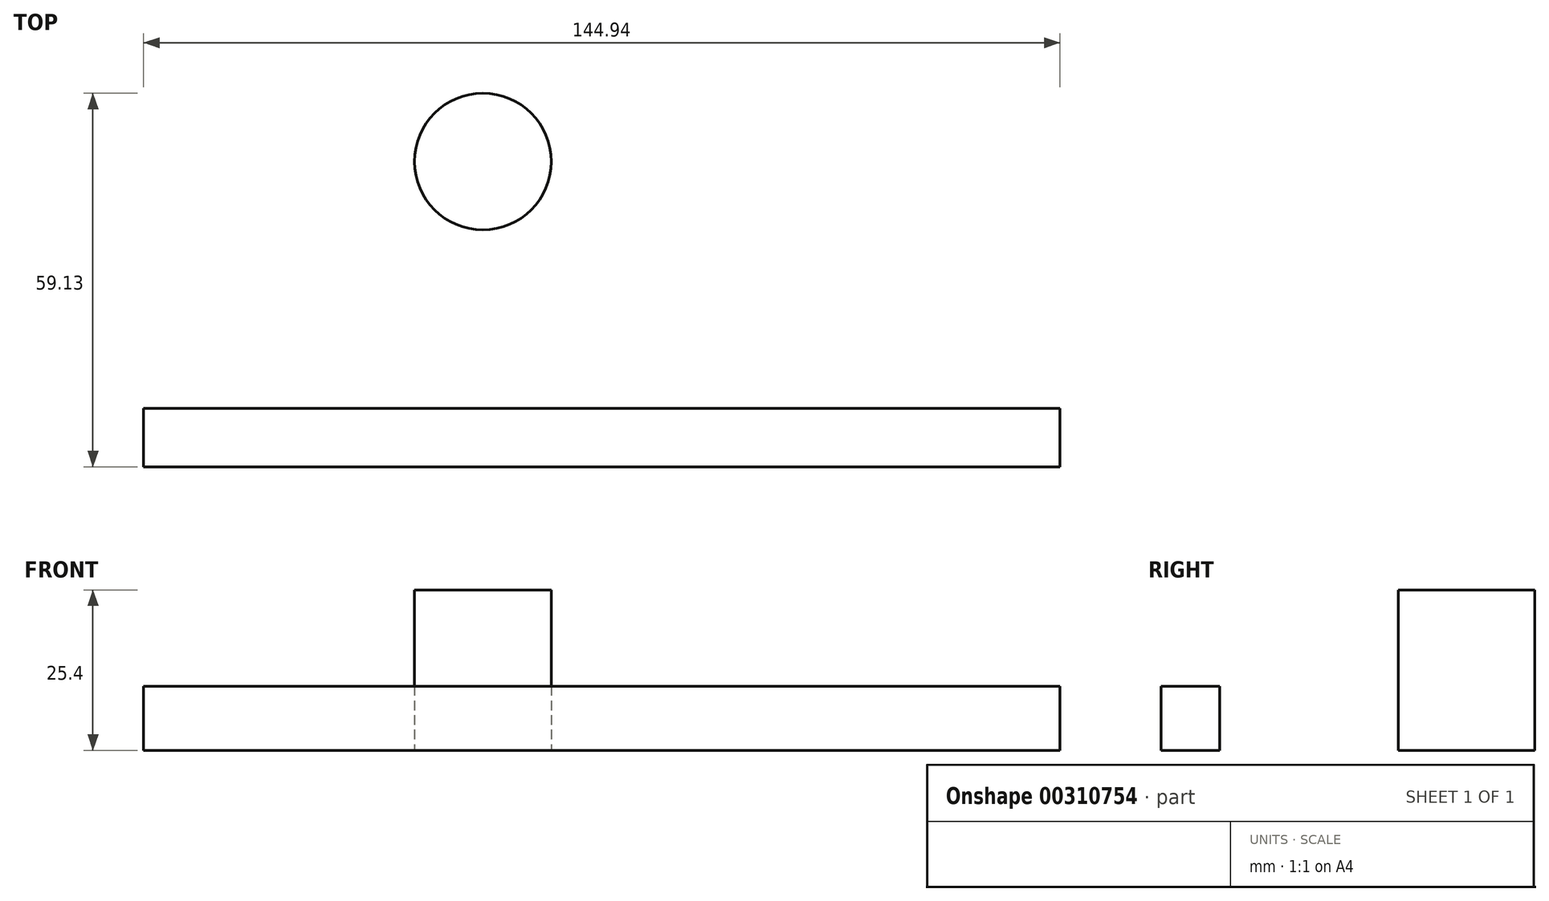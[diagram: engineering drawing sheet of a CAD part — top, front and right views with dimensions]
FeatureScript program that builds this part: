
annotation { "Feature Type Name" : "Feature", "Feature Type Description" : "" }
export const myFeature = defineFeature(function(context is Context, id is Id, definition is map)
    precondition{}
    {
        {
            var Q0;
            Q0=qCreatedBy(makeId("Top.planeOp"),FACE);
            var sketch = newSketch(context, id + "F0", { "sketchPlane" : qUnion([Q0])});
            skLineSegment(sketch, "E0.bottom", {"start": v(-72.47, 4.63) * mm, "end": v(72.47, 4.63) * mm});
            skLineSegment(sketch, "E0.top", {"start": v(-72.47, -4.63) * mm, "end": v(72.47, -4.63) * mm});
            skLineSegment(sketch, "E0.left", {"start": v(-72.47, 4.63) * mm, "end": v(-72.47, -4.63) * mm});
            skLineSegment(sketch, "E0.right", {"start": v(72.47, 4.63) * mm, "end": v(72.47, -4.63) * mm});
            skCircle(sketch, "E1", {"center": v(-18.8, 43.7) * mm, "radius": 10.8 * mm});
            skSolve(sketch);
        }
        {
            var Q0;
            Q0=makeQuery(id+"F0.imprint","IMPRINT",FACE,{"disambiguationData":[TD([[makeQuery(id+"F0.imprint","IMPRINT",EDGE,{"derivedFrom":sQuery(id+"F0.wireOp",EDGE,"E0.bottom")}),-1.0]])]});
            var Q1;
            Q1=sQuery(id+"F0.wireOp",EDGE,"E0.bottom");
            var Q2;
            Q2=sQuery(id+"F0.wireOp",EDGE,"E0.top");
            var Q3;
            Q3=sQuery(id+"F0.wireOp",EDGE,"E0.left");
            var Q4;
            Q4=sQuery(id+"F0.wireOp",EDGE,"E0.right");
            extrude(context, id + "F1", {"entities" : qUnion([Q0]), "surfaceEntities" : qUnion([Q1, Q2, Q3, Q4]), "depth" : 10.16 * mm});
        }
        {
            var Q0;
            Q0=makeQuery(id+"F0.imprint","IMPRINT",FACE,{"disambiguationData":[TD([[makeQuery(id+"F0.imprint","IMPRINT",EDGE,{"derivedFrom":sQuery(id+"F0.wireOp",EDGE,"E1")}),1.0]])]});
            extrude(context, id + "F2", {"entities" : qUnion([Q0]), "depth" : 25.4 * mm});
        }
    });
